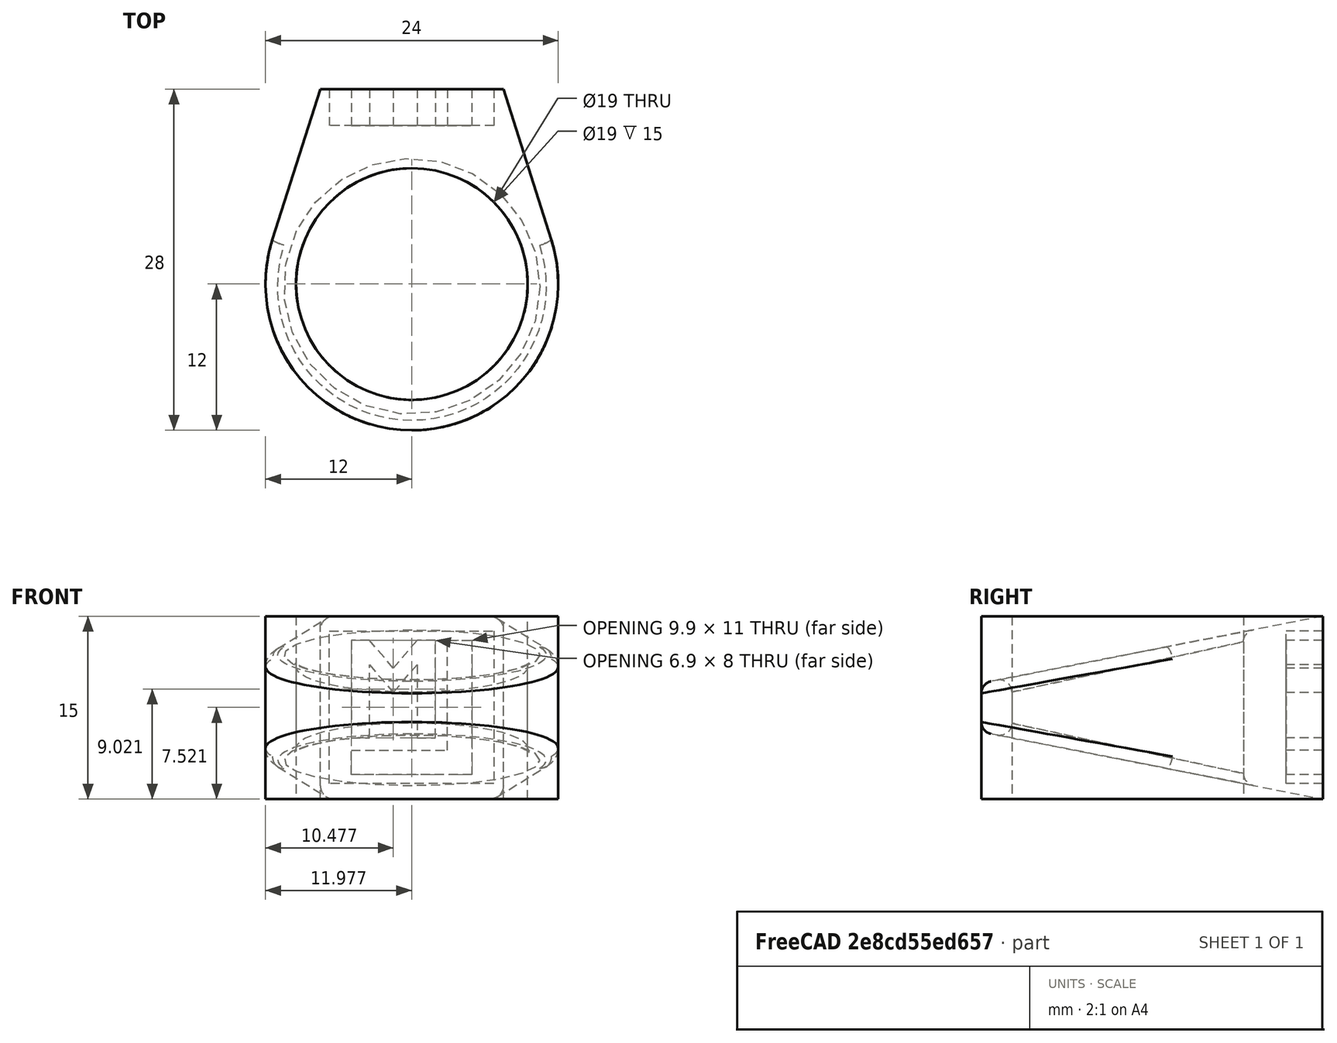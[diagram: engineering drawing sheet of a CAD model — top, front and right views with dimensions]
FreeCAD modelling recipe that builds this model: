
FCSTD DOCUMENT  (FreeCAD 0.21R33771 (Git))
Label: SignetRing
License: All rights reserved
LicenseURL: https://en.wikipedia.org/wiki/All_rights_reserved
objects: Sketcher::SketchObject×3, PartDesign::Pad×3, PartDesign::Body×3, PartDesign::Boolean×2, PartDesign::Fillet×1, Mesh::Feature×1
note: 16 computed .brp shape members not serialized (recipe doc carries the construction recipe); baked Part::Feature solids carry a one-line shape summary decoded from their .brp

FEATURE [Sketcher::SketchObject] Sketch
  FullyConstrained = true
  MapMode = 5
  Support = -> [XY_Plane]
  sketch-geometry (7):
    g0: Circle CenterX=1e-16 CenterY=12 CenterZ=0 NormalX=0 NormalY=0 NormalZ=1 AngleXU=0 Radius=9.5
    g1: LineSegment StartX=11.425 StartY=15.6701 StartZ=0 EndX=7.5 EndY=28 EndZ=0
    g2: LineSegment StartX=-7.5 StartY=28 StartZ=0 EndX=7.5 EndY=28 EndZ=0
    g3: LineSegment StartX=-7.5 StartY=28 StartZ=0 EndX=-11.425 EndY=15.6701 EndZ=0
    g4: GeomPoint X=0 Y=28 Z=0
    g5: ArcOfCircle CenterX=1e-16 CenterY=12 CenterZ=0 NormalX=0 NormalY=0 NormalZ=1 AngleXU=0 Radius=12 StartAngle=2.83077 EndAngle=6.594
    g6: GeomPoint X=0 Y=28 Z=0
  constraints (18):
    c: Diameter(g0) = 19
    c: Coincident(g2,g1)
    c: Horizontal(g2)
    c: Coincident(g3,g2)
    c: PointOnObject(g4,g2)
    c: DistanceY(g0,g4) = 16
    c: Symmetric(g1,g3,g-2)
    c: PointOnObject(g4,g-2)
    c: Coincident(g5,g0)
    c: Coincident(g5,g3)
    c: Diameter(g5) = 24
    c: Tangent(g5,g-1)
    c: Coincident(g1,g5)
    c: PointOnObject(g6,g2)
    c: PointOnObject(g6,g-2)
    c: DistanceX(g2,g4) = 7.5
    c: DistanceX(g4,g1) = 7.5
    c: DistanceX(g3,g1) = 22.85
FEATURE [PartDesign::Pad] Pad
  Direction = (0,0,1)
  Length = 15
  Length2 = 10
  Profile = -> Sketch
  ReferenceAxis = -> Sketch [N_Axis]
  Type = 0
FEATURE [PartDesign::Body] Body  label="Planta"
  Group = -> [Sketch,Pad]
  Origin = -> Origin
  Tip = -> Pad
FEATURE [Sketcher::SketchObject] Sketch001
  FullyConstrained = true
  MapMode = 5
  Placement = pos=(0,0,0) rot=(0.57735,0.57735,0.57735;2.0944rad)
  Support = -> [YZ_Plane001]
  sketch-geometry (4):
    g0: LineSegment StartX=28 StartY=15 StartZ=0 EndX=28 EndY=0 EndZ=0
    g1: LineSegment StartX=0 StartY=9.50154 StartZ=0 EndX=0 EndY=5.50154 EndZ=0
    g2: LineSegment StartX=28 StartY=15 StartZ=0 EndX=0 EndY=9.50154 EndZ=0
    g3: LineSegment StartX=28 StartY=0 StartZ=0 EndX=0 EndY=5.50154 EndZ=0
  constraints (12):
    c: Vertical(g0)
    c: PointOnObject(g1,g-2)
    c: Vertical(g1)
    c: Coincident(g2,g0)
    c: Coincident(g2,g1)
    c: Coincident(g3,g0)
    c: Coincident(g3,g1)
    c: DistanceY(g0,g0) = 15
    c: DistanceY(g1,g1) = 4
    c: PointOnObject(g0,g-1)
    c: DistanceX(g1,g0) = 28
    c: Angle(g2,g0) = 1.37689
FEATURE [PartDesign::Pad] Pad001
  Direction = (1,-2e-16,3e-16)
  Length = 14
  Length2 = 14
  Placement = pos=(0,0,0) rot=(1,1,1;2.0944rad)
  Profile = -> Sketch001
  ReferenceAxis = -> Sketch001 [N_Axis]
  Type = 4
FEATURE [PartDesign::Boolean] Boolean
  BaseFeature = -> Pad001
  Group = -> [Body]
  Type = 2
FEATURE [Sketcher::SketchObject] Sketch003
  FullyConstrained = true
  Placement = pos=(0,28,0) rot=(1,0,0;1.5708rad)
  sketch-geometry (22):
    g0: LineSegment StartX=6.72703 StartY=1.27069 StartZ=0 EndX=-6.77297 EndY=1.27069 EndZ=0
    g1: LineSegment StartX=-6.77297 StartY=1.27069 StartZ=0 EndX=-6.77297 EndY=13.7707 EndZ=0
    g2: LineSegment StartX=-6.77297 StartY=13.7707 StartZ=0 EndX=6.72703 EndY=13.7707 EndZ=0
    g3: LineSegment StartX=6.72703 StartY=13.7707 StartZ=0 EndX=6.72703 EndY=1.27069 EndZ=0
    g4: LineSegment StartX=4.92703 StartY=13.0207 StartZ=0 EndX=4.92703 EndY=2.02069 EndZ=0
    g5: LineSegment StartX=4.92703 StartY=2.02069 StartZ=0 EndX=-4.97297 EndY=2.02069 EndZ=0
    g6: LineSegment StartX=-4.97297 StartY=2.02069 StartZ=0 EndX=-4.97297 EndY=4.02069 EndZ=0
    g7: LineSegment StartX=-4.97297 StartY=4.02069 StartZ=0 EndX=2.92703 EndY=4.02069 EndZ=0
    g8: LineSegment StartX=2.92703 StartY=4.02069 StartZ=0 EndX=2.92703 EndY=13.0207 EndZ=0
    g9: LineSegment StartX=2.92703 StartY=13.0207 StartZ=0 EndX=4.92703 EndY=13.0207 EndZ=0
    g10: LineSegment StartX=1.92703 StartY=5.02069 StartZ=0 EndX=1.92703 EndY=13.0207 EndZ=0
    g11: LineSegment StartX=1.92703 StartY=13.0207 StartZ=0 EndX=0.427034 EndY=13.0207 EndZ=0
    g12: LineSegment StartX=0.427034 StartY=13.0207 StartZ=0 EndX=-1.52297 EndY=10.7409 EndZ=0
    g13: LineSegment StartX=-1.52297 StartY=10.7409 StartZ=0 EndX=-3.47297 EndY=13.0207 EndZ=0
    g14: LineSegment StartX=-3.47297 StartY=13.0207 StartZ=0 EndX=-4.97297 EndY=13.0207 EndZ=0
    g15: LineSegment StartX=-4.97297 StartY=13.0207 StartZ=0 EndX=-4.97297 EndY=5.02069 EndZ=0
    g16: LineSegment StartX=-4.97297 StartY=5.02069 StartZ=0 EndX=-3.47297 EndY=5.02069 EndZ=0
    g17: LineSegment StartX=-3.47297 StartY=5.02069 StartZ=0 EndX=-3.47297 EndY=11.0207 EndZ=0
    g18: LineSegment StartX=-3.47297 StartY=11.0207 StartZ=0 EndX=-1.52297 EndY=8.74089 EndZ=0
    g19: LineSegment StartX=-1.52297 StartY=8.74089 StartZ=0 EndX=0.427034 EndY=11.0207 EndZ=0
    g20: LineSegment StartX=0.427034 StartY=11.0207 StartZ=0 EndX=0.427034 EndY=5.02069 EndZ=0
    g21: LineSegment StartX=0.427034 StartY=5.02069 StartZ=0 EndX=1.92703 EndY=5.02069 EndZ=0
  constraints (66):
    c: Coincident(g0,g1)
    c: Coincident(g1,g2)
    c: Coincident(g2,g3)
    c: Coincident(g3,g0)
    c: Horizontal(g0)
    c: Horizontal(g2)
    c: Vertical(g1)
    c: Vertical(g3)
    c: DistanceX(g1,g2) = 13.5
    c: DistanceY(g0,g2) = 12.5
    c: Vertical(g4)
    c: Coincident(g5,g4)
    c: Horizontal(g5)
    c: Coincident(g6,g5)
    c: Vertical(g6)
    c: Coincident(g7,g6)
    c: Horizontal(g7)
    c: Coincident(g8,g7)
    c: Vertical(g8)
    c: Coincident(g9,g8)
    c: Coincident(g9,g4)
    c: Horizontal(g9)
    c: DistanceX(g0) = 6.72703
    c: DistanceY(g0) = 1.27069
    c: DistanceX(g8,g4) = 2
    c: DistanceY(g5,g6) = 2
    c: Vertical(g10)
    c: Coincident(g10,g11)
    c: Horizontal(g11)
    c: Coincident(g11,g12)
    c: Coincident(g12,g13)
    c: Coincident(g13,g14)
    c: Horizontal(g14)
    c: Coincident(g14,g15)
    c: Vertical(g15)
    c: Coincident(g15,g16)
    c: Horizontal(g16)
    c: Coincident(g16,g17)
    c: Vertical(g17)
    c: Coincident(g17,g18)
    c: Coincident(g18,g19)
    c: Coincident(g19,g20)
    c: Vertical(g20)
    c: Coincident(g20,g21)
    c: Coincident(g21,g10)
    c: Horizontal(g21)
    c: DistanceX(g11,g10) = 1.5
    c: DistanceX(g21,g21) = 1.5
    c: DistanceX(g16,g16) = 1.5
    c: DistanceX(g14,g14) = 1.5
    c: DistanceY(g4,g4) = 11
    c: DistanceY(g10,g10) = 8
    c: DistanceY(g15,g15) = 8
    c: DistanceX(g6,g7) = 7.9
    c: DistanceY(g17,g13) = 2
    c: DistanceY(g19,g11) = 2
    c: Equal(g12,g19)
    c: Equal(g13,g18)
    c: Equal(g12,g13)
    c: Distance(g13,g12) = 3
    c: DistanceX(g0,g5) = 1.8
    c: DistanceY(g0,g4) = 0.75
    c: DistanceY(g10,g2) = 0.75
    c: DistanceY(g14,g1) = 0.75
    c: DistanceX(g0,g15) = 1.8
    c: DistanceX(g10,g8) = 1
FEATURE [PartDesign::Pad] Pad002
  Direction = (0,-1,2e-16)
  Length = 3
  Length2 = 10
  Placement = pos=(0,28,0) rot=(1,0,0;1.5708rad)
  Profile = -> Sketch003
  ReferenceAxis = -> Sketch003 [N_Axis]
  Type = 0
FEATURE [PartDesign::Body] Body002  label="Design"
  Group = -> [Sketch003,Pad002]
  Origin = -> Origin002
  Tip = -> Pad002
FEATURE [PartDesign::Boolean] Boolean001
  BaseFeature = -> Boolean
  Group = -> [Body002]
  Type = 1
FEATURE [PartDesign::Fillet] Fillet
  Base = -> Boolean001 [Edge6,Edge2,Edge3,Edge12,Edge21,Edge14,Edge4,Edge1,Edge7,Edge10]
  BaseFeature = -> Boolean001
  Radius = 1
  SupportTransform = false
  UseAllEdges = false
FEATURE [PartDesign::Body] Body001  label="Perfil"
  Group = -> [Sketch001,Pad001,Boolean,Boolean001,Fillet]
  Origin = -> Origin001
  Tip = -> Fillet
FEATURE [Mesh::Feature] Mesh  label="Perfil (Meshed)"
